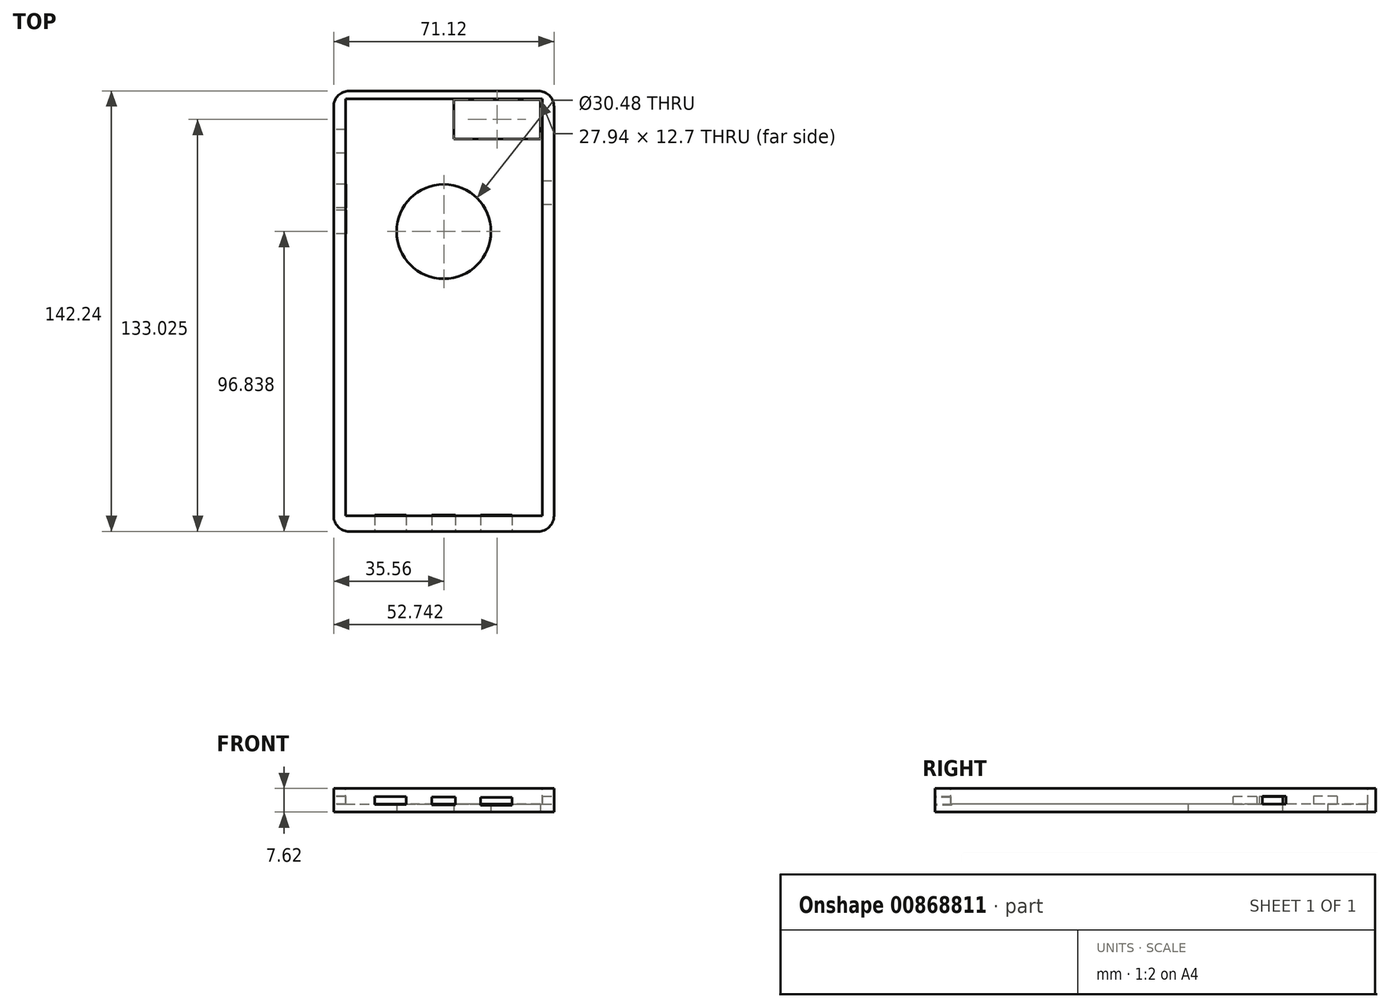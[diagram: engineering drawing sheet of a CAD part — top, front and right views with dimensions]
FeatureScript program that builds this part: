
annotation { "Feature Type Name" : "Feature", "Feature Type Description" : "" }
export const myFeature = defineFeature(function(context is Context, id is Id, definition is map)
    precondition{}
    {
        {
            var Q0;
            Q0=qCreatedBy(makeId("Top.planeOp"),FACE);
            var sketch = newSketch(context, id + "F0", { "sketchPlane" : qUnion([Q0])});
            skLineSegment(sketch, "E0.bottom", {"start": v(-35.56, 84.55) * mm, "end": v(35.56, 84.55) * mm});
            skLineSegment(sketch, "E0.top", {"start": v(-35.56, -57.69) * mm, "end": v(35.56, -57.69) * mm});
            skLineSegment(sketch, "E0.left", {"start": v(-35.56, 84.55) * mm, "end": v(-35.56, -57.69) * mm});
            skLineSegment(sketch, "E0.right", {"start": v(35.56, 84.55) * mm, "end": v(35.56, -57.69) * mm});
            skSolve(sketch);
        }
        {
            var Q0;
            Q0 = qSketchRegion(id + "F0", true);
            extrude(context, id + "F1", {"entities" : qUnion([Q0]), "endBound" : BoundingType.SYMMETRIC, "oppositeDirection" : true, "depth" : 7.62 * mm, "offsetDistance" : 25.4 * mm});
        }
        {
            var Q0;
            Q0=makeQuery(id+"F1.opExtrude","CAP_FACE",FACE,{"disambiguationData":[OSD([sQuery(id+"F0.wireOp",EDGE,"E0.bottom"),sQuery(id+"F0.wireOp",EDGE,"E0.top"),sQuery(id+"F0.wireOp",EDGE,"E0.left"),sQuery(id+"F0.wireOp",EDGE,"E0.right")])],"isStart":true});
            var sketch = newSketch(context, id + "F2", { "sketchPlane" : qUnion([Q0])});
            skLineSegment(sketch, "E1.bottom", {"start": v(-31.68, 81.96) * mm, "end": v(31.82, 81.96) * mm});
            skLineSegment(sketch, "E1.top", {"start": v(-31.68, -52.66) * mm, "end": v(31.82, -52.66) * mm});
            skLineSegment(sketch, "E1.left", {"start": v(-31.68, 81.96) * mm, "end": v(-31.68, -52.66) * mm});
            skLineSegment(sketch, "E1.right", {"start": v(31.82, 81.96) * mm, "end": v(31.82, -52.66) * mm});
            skSolve(sketch);
        }
        {
            var Q0;
            Q0=makeQuery(id+"F2.imprint","IMPRINT",FACE,{"disambiguationData":[TD([[makeQuery(id+"F2.imprint","IMPRINT",EDGE,{"derivedFrom":sQuery(id+"F2.wireOp",EDGE,"E1.bottom")}),-1.0]])]});
            extrude(context, id + "F3", {"entities" : qUnion([Q0]), "operationType" : NewBodyOperationType.REMOVE, "oppositeDirection" : true, "depth" : 5.08 * mm, "offsetDistance" : 25.4 * mm});
        }
        {
            var Q0;
            Q0=makeQuery(id+"F1.opExtrude","SWEPT_FACE",FACE,{"disambiguationData":[OSD([sQuery(id+"F0.wireOp",EDGE,"E0.top")])]});
            var sketch = newSketch(context, id + "F4", { "sketchPlane" : qUnion([Q0])});
            skLineSegment(sketch, "E2.bottom", {"start": v(-22.24, 1.2) * mm, "end": v(-12.08, 1.2) * mm});
            skLineSegment(sketch, "E2.top", {"start": v(-22.24, -1.33) * mm, "end": v(-12.08, -1.33) * mm});
            skLineSegment(sketch, "E2.left", {"start": v(-22.24, 1.2) * mm, "end": v(-22.24, -1.33) * mm});
            skLineSegment(sketch, "E2.right", {"start": v(-12.08, 1.2) * mm, "end": v(-12.08, -1.33) * mm});
            skLineSegment(sketch, "E3.bottom", {"start": v(11.9, 1) * mm, "end": v(22.07, 1) * mm});
            skLineSegment(sketch, "E3.top", {"start": v(11.9, -1.55) * mm, "end": v(22.07, -1.55) * mm});
            skLineSegment(sketch, "E3.left", {"start": v(11.9, 1) * mm, "end": v(11.9, -1.55) * mm});
            skLineSegment(sketch, "E3.right", {"start": v(22.07, 1) * mm, "end": v(22.07, -1.55) * mm});
            skSolve(sketch);
        }
        {
            var Q0;
            Q0 = qSketchRegion(id + "F4", true);
            extrude(context, id + "F5", {"entities" : qUnion([Q0]), "operationType" : NewBodyOperationType.REMOVE, "oppositeDirection" : true, "depth" : 5.33 * mm, "offsetDistance" : 25.4 * mm});
        }
        {
            var Q0;
            Q0=makeQuery(id+"F1.opExtrude","SWEPT_FACE",FACE,{"disambiguationData":[OSD([sQuery(id+"F0.wireOp",EDGE,"E0.top")])]});
            var sketch = newSketch(context, id + "F6", { "sketchPlane" : qUnion([Q0])});
            skLineSegment(sketch, "E4.bottom", {"start": v(3.8, -1.43) * mm, "end": v(-3.82, -1.43) * mm});
            skLineSegment(sketch, "E4.top", {"start": v(3.8, 1.11) * mm, "end": v(-3.82, 1.11) * mm});
            skLineSegment(sketch, "E4.left", {"start": v(3.8, -1.43) * mm, "end": v(3.8, 1.11) * mm});
            skLineSegment(sketch, "E4.right", {"start": v(-3.82, -1.43) * mm, "end": v(-3.82, 1.11) * mm});
            skSolve(sketch);
        }
        {
            var Q0;
            Q0 = qSketchRegion(id + "F6", true);
            extrude(context, id + "F7", {"entities" : qUnion([Q0]), "operationType" : NewBodyOperationType.REMOVE, "oppositeDirection" : true, "depth" : 5.33 * mm, "offsetDistance" : 25.4 * mm});
        }
        {
            var Q0;
            Q0=makeQuery(id+"F1.opExtrude","SWEPT_FACE",FACE,{"disambiguationData":[OSD([sQuery(id+"F0.wireOp",EDGE,"E0.right")])]});
            var sketch = newSketch(context, id + "F8", { "sketchPlane" : qUnion([Q0])});
            skLineSegment(sketch, "E5.bottom", {"start": v(55.6, -1.25) * mm, "end": v(47.97, -1.25) * mm});
            skLineSegment(sketch, "E5.top", {"start": v(55.6, 1.29) * mm, "end": v(47.97, 1.29) * mm});
            skLineSegment(sketch, "E5.left", {"start": v(55.6, -1.25) * mm, "end": v(55.6, 1.29) * mm});
            skLineSegment(sketch, "E5.right", {"start": v(47.97, -1.25) * mm, "end": v(47.97, 1.29) * mm});
            skSolve(sketch);
        }
        {
            var Q0;
            Q0 = qSketchRegion(id + "F8", true);
            extrude(context, id + "F9", {"entities" : qUnion([Q0]), "operationType" : NewBodyOperationType.REMOVE, "oppositeDirection" : true, "depth" : 4.57 * mm, "offsetDistance" : 25.4 * mm});
        }
        {
            var Q0;
            Q0=makeQuery(id+"F1.opExtrude","SWEPT_FACE",FACE,{"disambiguationData":[OSD([sQuery(id+"F0.wireOp",EDGE,"E0.left")])]});
            var sketch = newSketch(context, id + "F10", { "sketchPlane" : qUnion([Q0])});
            skLineSegment(sketch, "E6.bottom", {"start": v(-72.02, 1.36) * mm, "end": v(-64.4, 1.36) * mm});
            skLineSegment(sketch, "E6.top", {"start": v(-72.02, -1.18) * mm, "end": v(-64.4, -1.18) * mm});
            skLineSegment(sketch, "E6.left", {"start": v(-72.02, 1.36) * mm, "end": v(-72.02, -1.18) * mm});
            skLineSegment(sketch, "E6.right", {"start": v(-64.4, 1.36) * mm, "end": v(-64.4, -1.18) * mm});
            skSolve(sketch);
        }
        {
            var Q0;
            Q0 = qSketchRegion(id + "F10", true);
            extrude(context, id + "F11", {"entities" : qUnion([Q0]), "operationType" : NewBodyOperationType.REMOVE, "oppositeDirection" : true, "depth" : 4.06 * mm, "offsetDistance" : 25.4 * mm});
        }
        {
            var Q0;
            Q0=makeQuery(id+"F1.opExtrude","SWEPT_FACE",FACE,{"disambiguationData":[OSD([sQuery(id+"F0.wireOp",EDGE,"E0.left")])]});
            var sketch = newSketch(context, id + "F12", { "sketchPlane" : qUnion([Q0])});
            skLineSegment(sketch, "E7.bottom", {"start": v(-54.49, 1.24) * mm, "end": v(-46.87, 1.24) * mm});
            skLineSegment(sketch, "E7.top", {"start": v(-54.49, -1.3) * mm, "end": v(-46.87, -1.3) * mm});
            skLineSegment(sketch, "E7.left", {"start": v(-54.49, 1.24) * mm, "end": v(-54.49, -1.3) * mm});
            skLineSegment(sketch, "E7.right", {"start": v(-46.87, 1.24) * mm, "end": v(-46.87, -1.3) * mm});
            skLineSegment(sketch, "E8.bottom", {"start": v(-46.1, 1.24) * mm, "end": v(-38.47, 1.24) * mm});
            skLineSegment(sketch, "E8.top", {"start": v(-46.1, -1.3) * mm, "end": v(-38.47, -1.3) * mm});
            skLineSegment(sketch, "E8.left", {"start": v(-46.1, 1.24) * mm, "end": v(-46.1, -1.3) * mm});
            skLineSegment(sketch, "E8.right", {"start": v(-38.47, 1.24) * mm, "end": v(-38.47, -1.3) * mm});
            skSolve(sketch);
        }
        {
            var Q0;
            Q0 = qSketchRegion(id + "F12", true);
            extrude(context, id + "F13", {"entities" : qUnion([Q0]), "operationType" : NewBodyOperationType.REMOVE, "oppositeDirection" : true, "depth" : 4.06 * mm, "offsetDistance" : 25.4 * mm});
        }
        {
            var Q0;
            Q0=makeQuery(id+"F1.opExtrude","CAP_FACE",FACE,{"disambiguationData":[OSD([sQuery(id+"F0.wireOp",EDGE,"E0.bottom"),sQuery(id+"F0.wireOp",EDGE,"E0.top"),sQuery(id+"F0.wireOp",EDGE,"E0.left"),sQuery(id+"F0.wireOp",EDGE,"E0.right")])],"isStart":false});
            var sketch = newSketch(context, id + "F14", { "sketchPlane" : qUnion([Q0])});
            skLineSegment(sketch, "E9.bottom", {"start": v(3.21, -81.69) * mm, "end": v(31.15, -81.69) * mm});
            skLineSegment(sketch, "E9.top", {"start": v(3.21, -68.99) * mm, "end": v(31.15, -68.99) * mm});
            skLineSegment(sketch, "E9.left", {"start": v(3.21, -81.69) * mm, "end": v(3.21, -68.99) * mm});
            skLineSegment(sketch, "E9.right", {"start": v(31.15, -81.69) * mm, "end": v(31.15, -68.99) * mm});
            skSolve(sketch);
        }
        {
            var Q0;
            Q0 = qSketchRegion(id + "F14", true);
            extrude(context, id + "F15", {"entities" : qUnion([Q0]), "operationType" : NewBodyOperationType.REMOVE, "oppositeDirection" : true, "depth" : 4.06 * mm, "offsetDistance" : 25.4 * mm});
        }
        {
            var Q0;
            Q0=makeQuery(id+"F1.opExtrude","CAP_FACE",FACE,{"disambiguationData":[OSD([sQuery(id+"F0.wireOp",EDGE,"E0.bottom"),sQuery(id+"F0.wireOp",EDGE,"E0.top"),sQuery(id+"F0.wireOp",EDGE,"E0.left"),sQuery(id+"F0.wireOp",EDGE,"E0.right")])],"isStart":false});
            var sketch = newSketch(context, id + "F16", { "sketchPlane" : qUnion([Q0])});
            skCircle(sketch, "E10", {"center": v(0, -39.15) * mm, "radius": 15.24 * mm});
            skSolve(sketch);
        }
        {
            var Q0;
            Q0 = qSketchRegion(id + "F16", true);
            extrude(context, id + "F17", {"entities" : qUnion([Q0]), "operationType" : NewBodyOperationType.REMOVE, "oppositeDirection" : true, "depth" : 4.06 * mm, "offsetDistance" : 25.4 * mm});
        }
        {
            var Q0;
            Q0=makeQuery(id+"F1.opExtrude","SWEPT_EDGE",EDGE,{"disambiguationData":[OSD([sQuery(id+"F0.wireOp",EDGE,"E0.top"),sQuery(id+"F0.wireOp",EDGE,"E0.right")])]});
            var Q1;
            Q1=makeQuery(id+"F1.opExtrude","SWEPT_EDGE",EDGE,{"disambiguationData":[OSD([sQuery(id+"F0.wireOp",EDGE,"E0.top"),sQuery(id+"F0.wireOp",EDGE,"E0.left")])]});
            var Q2;
            Q2=makeQuery(id+"F1.opExtrude","SWEPT_EDGE",EDGE,{"disambiguationData":[OSD([sQuery(id+"F0.wireOp",EDGE,"E0.bottom"),sQuery(id+"F0.wireOp",EDGE,"E0.left")])]});
            var Q3;
            Q3=makeQuery(id+"F1.opExtrude","SWEPT_EDGE",EDGE,{"disambiguationData":[OSD([sQuery(id+"F0.wireOp",EDGE,"E0.bottom"),sQuery(id+"F0.wireOp",EDGE,"E0.right")])]});
            fillet(context, id + "F18", {"entities" : qUnion([Q0, Q1, Q2, Q3]), "radius" : 5.08 * mm, "tangentPropagation" : true, "allowEdgeOverflow" : false});
        }
    });
